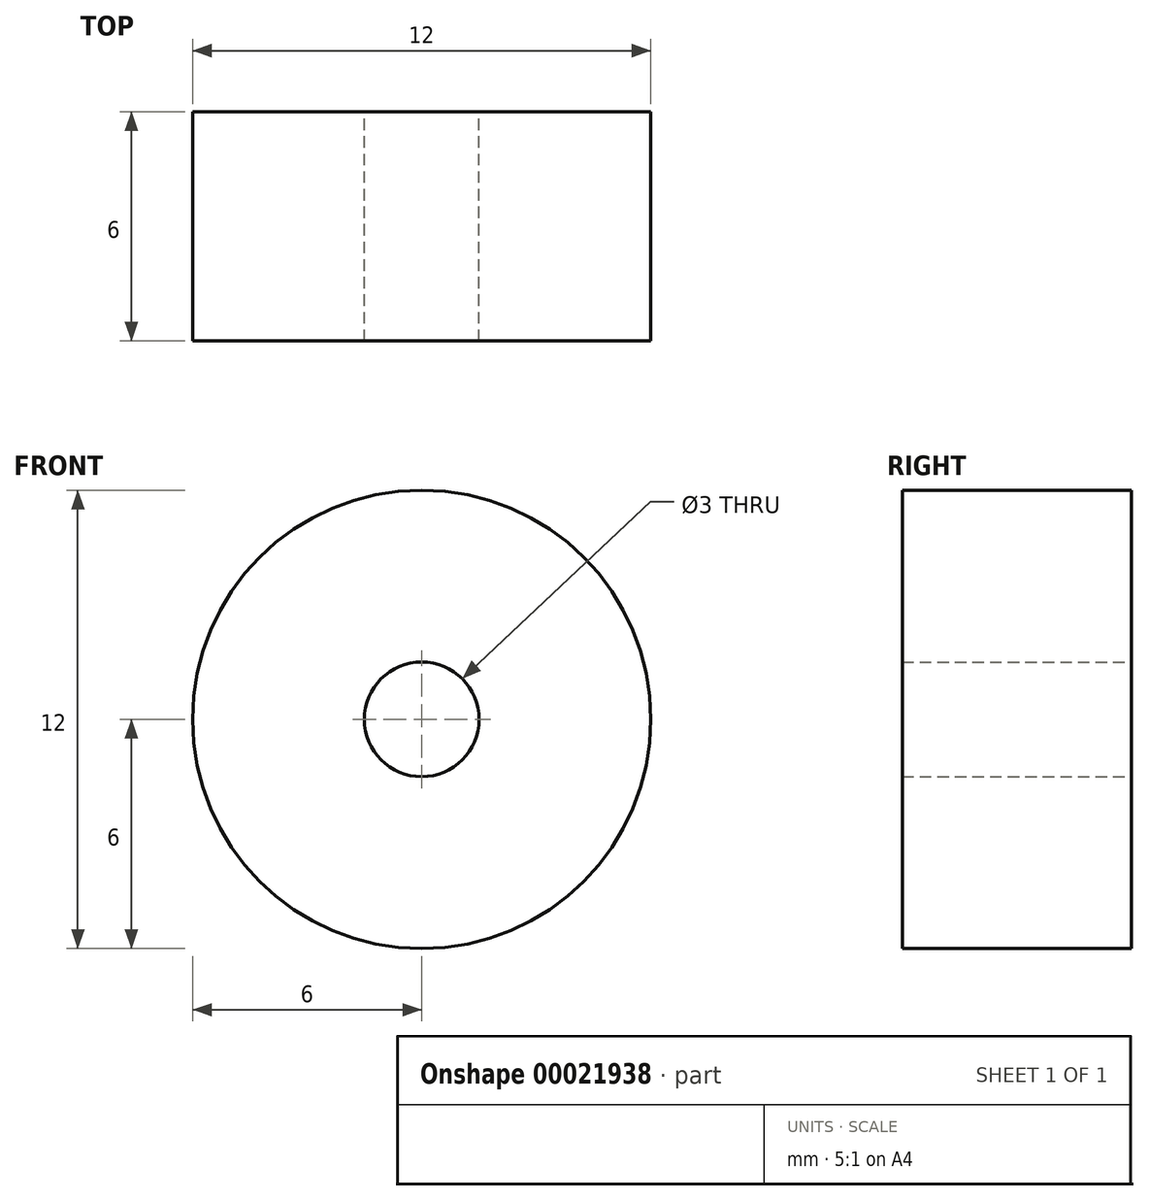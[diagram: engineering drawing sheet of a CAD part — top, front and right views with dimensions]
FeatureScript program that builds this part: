
annotation { "Feature Type Name" : "Feature", "Feature Type Description" : "" }
export const myFeature = defineFeature(function(context is Context, id is Id, definition is map)
    precondition{}
    {
        {
            var Q0;
            Q0=qCreatedBy(makeId("Front.planeOp"),FACE);
            var sketch = newSketch(context, id + "F0", { "sketchPlane" : qUnion([Q0])});
            skCircle(sketch, "E0", {"center": v(0, 0) * mm, "radius": 6 * mm});
            skCircle(sketch, "E1", {"center": v(0, 0) * mm, "radius": 1.5 * mm});
            skSolve(sketch);
        }
        {
            var Q0;
            Q0=makeQuery(id+"F0.imprint","IMPRINT",FACE,{"disambiguationData":[TD([[makeQuery(id+"F0.imprint","IMPRINT",EDGE,{"derivedFrom":sQuery(id+"F0.wireOp",EDGE,"E0")}),1.0]])]});
            extrude(context, id + "F1", {"entities" : qUnion([Q0]), "depth" : 6 * mm});
        }
    });
